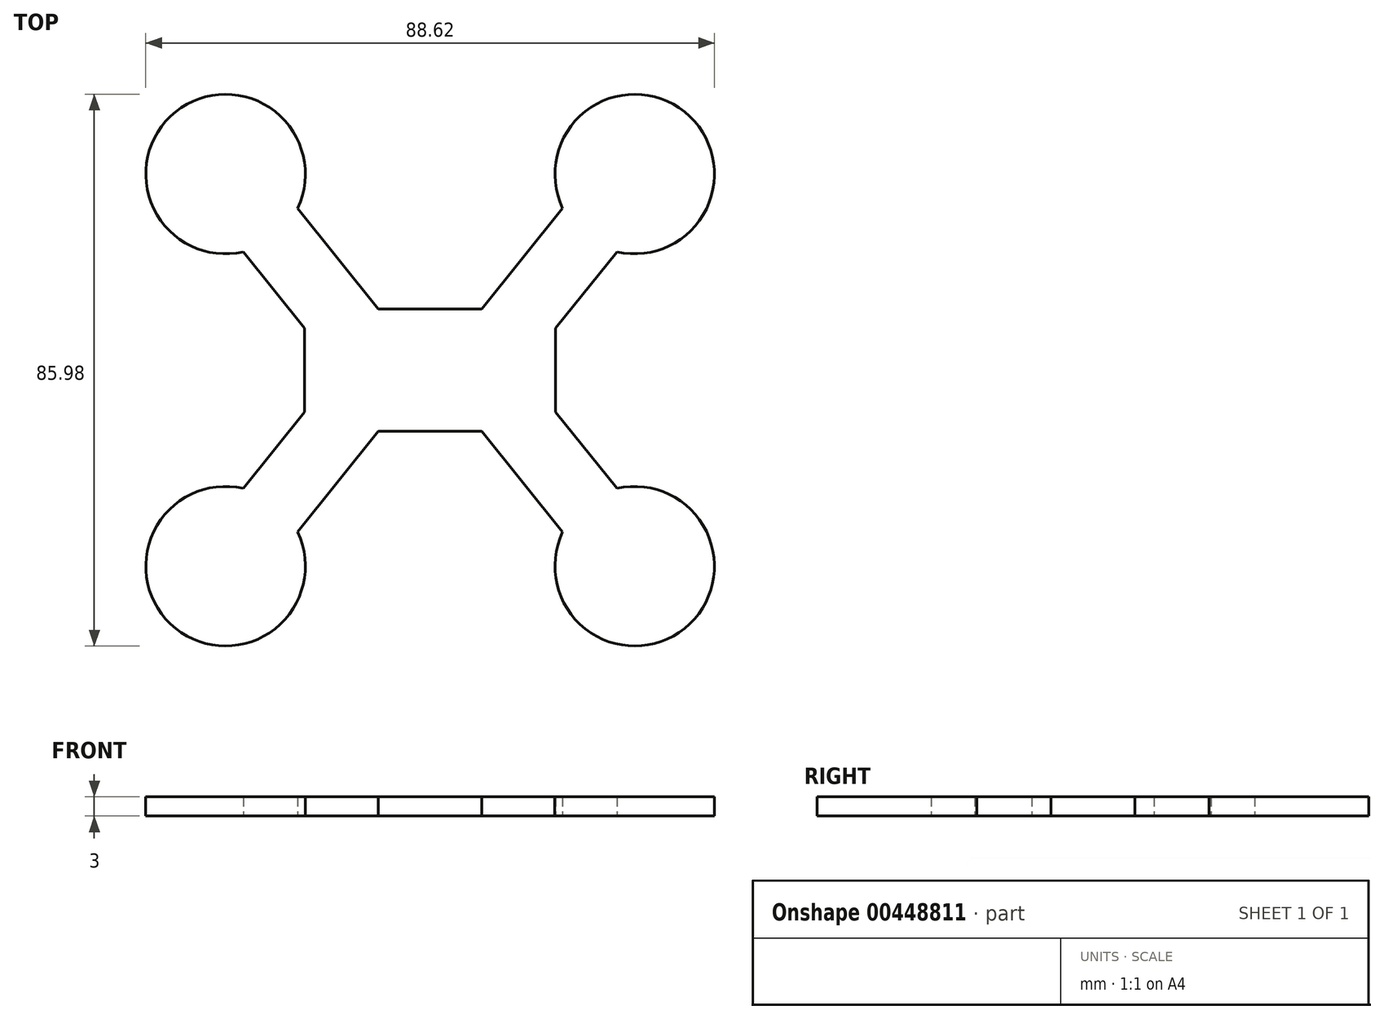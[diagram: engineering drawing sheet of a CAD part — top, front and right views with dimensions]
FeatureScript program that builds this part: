
annotation { "Feature Type Name" : "Feature", "Feature Type Description" : "" }
export const myFeature = defineFeature(function(context is Context, id is Id, definition is map)
    precondition{}
    {
        {
            var Q0;
            Q0=qCreatedBy(makeId("Top.planeOp"),FACE);
            var sketch = newSketch(context, id + "F0", { "sketchPlane" : qUnion([Q0])});
            skLineSegment(sketch, "E0", {"start": v(8.05, 9.53) * mm, "end": v(27.64, 33.95) * mm});
            skLineSegment(sketch, "E1", {"start": v(27.64, 33.95) * mm, "end": v(36.11, 27.16) * mm});
            skLineSegment(sketch, "E2", {"start": v(36.11, 27.16) * mm, "end": v(19.57, 6.54) * mm});
            skLineSegment(sketch, "E3", {"start": v(19.57, 6.54) * mm, "end": v(8.05, 9.53) * mm});
            skCircle(sketch, "E4", {"center": v(31.88, 30.56) * mm, "radius": 12.43 * mm});
            skLineSegment(sketch, "E5.MirrorCS", {"start": v(-27.64, 33.95) * mm, "end": v(-36.11, 27.16) * mm});
            skLineSegment(sketch, "E6.MirrorCS", {"start": v(-8.05, 9.53) * mm, "end": v(-27.64, 33.95) * mm});
            skLineSegment(sketch, "E7.MirrorCS", {"start": v(-19.57, 6.54) * mm, "end": v(-8.05, 9.53) * mm});
            skLineSegment(sketch, "E8.MirrorCS", {"start": v(-36.11, 27.16) * mm, "end": v(-19.57, 6.54) * mm});
            skCircle(sketch, "E9.MirrorC", {"center": v(-31.88, 30.56) * mm, "radius": 12.43 * mm});
            skLineSegment(sketch, "E10.MirrorCS", {"start": v(27.64, -33.95) * mm, "end": v(36.11, -27.16) * mm});
            skCircle(sketch, "E11.MirrorC", {"center": v(31.88, -30.56) * mm, "radius": 12.43 * mm});
            skLineSegment(sketch, "E12.MirrorCS", {"start": v(19.57, -6.54) * mm, "end": v(8.05, -9.53) * mm});
            skLineSegment(sketch, "E13.MirrorCS", {"start": v(36.11, -27.16) * mm, "end": v(19.57, -6.54) * mm});
            skLineSegment(sketch, "E14.MirrorCS", {"start": v(8.05, -9.53) * mm, "end": v(27.64, -33.95) * mm});
            skLineSegment(sketch, "E15.MirrorCS", {"start": v(-27.64, -33.95) * mm, "end": v(-36.11, -27.16) * mm});
            skLineSegment(sketch, "E16.MirrorCS", {"start": v(-36.11, -27.16) * mm, "end": v(-19.57, -6.54) * mm});
            skLineSegment(sketch, "E17.MirrorCS", {"start": v(-19.57, -6.54) * mm, "end": v(-8.05, -9.53) * mm});
            skCircle(sketch, "E18.MirrorC", {"center": v(-31.88, -30.56) * mm, "radius": 12.43 * mm});
            skLineSegment(sketch, "E19.MirrorCS", {"start": v(-8.05, -9.53) * mm, "end": v(-27.64, -33.95) * mm});
            skLineSegment(sketch, "E20.bottom", {"start": v(-19.57, 6.54) * mm, "end": v(19.57, 6.54) * mm});
            skLineSegment(sketch, "E20.top", {"start": v(-19.57, -6.54) * mm, "end": v(19.57, -6.54) * mm});
            skLineSegment(sketch, "E20.left", {"start": v(-19.57, 6.54) * mm, "end": v(-19.57, -6.54) * mm});
            skLineSegment(sketch, "E20.right", {"start": v(19.57, 6.54) * mm, "end": v(19.57, -6.54) * mm});
            skLineSegment(sketch, "E21.bottom", {"start": v(-8.05, 9.53) * mm, "end": v(8.05, 9.53) * mm});
            skLineSegment(sketch, "E21.top", {"start": v(-8.05, -9.53) * mm, "end": v(8.05, -9.53) * mm});
            skLineSegment(sketch, "E21.left", {"start": v(-8.05, 9.53) * mm, "end": v(-8.05, -9.53) * mm});
            skLineSegment(sketch, "E21.right", {"start": v(8.05, 9.53) * mm, "end": v(8.05, -9.53) * mm});
            skSolve(sketch);
        }
        {
            var Q0;
            {var subQ0=sQuery(id+"F0.wireOp",EDGE,"E5.MirrorCS");Q0=makeQuery(id+"F0.imprint","IMPRINT",FACE,{"disambiguationData":[TD([[makeQuery(id+"F0.imprint","IMPRINT",EDGE,{"derivedFrom":subQ0}),-1.0]])]});}
            var Q1;
            {var subQ0=sQuery(id+"F0.wireOp",EDGE,"E5.MirrorCS");Q1=makeQuery(id+"F0.imprint","IMPRINT",FACE,{"disambiguationData":[TD([[makeQuery(id+"F0.imprint","IMPRINT",EDGE,{"derivedFrom":subQ0}),1.0]])]});}
            var Q2;
            {var subQ5=sQuery(id+"F0.wireOp",EDGE,"E7.MirrorCS");Q2=makeQuery(id+"F0.imprint","IMPRINT",FACE,{"disambiguationData":[TD([[makeQuery(id+"F0.imprint","IMPRINT",EDGE,{"derivedFrom":subQ5}),1.0]])]});}
            var Q3;
            {var subQ0=sQuery(id+"F0.wireOp",EDGE,"E1");Q3=makeQuery(id+"F0.imprint","IMPRINT",FACE,{"disambiguationData":[TD([[makeQuery(id+"F0.imprint","IMPRINT",EDGE,{"derivedFrom":subQ0}),1.0]])]});}
            var Q4;
            {var subQ0=sQuery(id+"F0.wireOp",EDGE,"E1");Q4=makeQuery(id+"F0.imprint","IMPRINT",FACE,{"disambiguationData":[TD([[makeQuery(id+"F0.imprint","IMPRINT",EDGE,{"derivedFrom":subQ0}),-1.0]])]});}
            var Q5;
            {var subQ5=sQuery(id+"F0.wireOp",EDGE,"E3");Q5=makeQuery(id+"F0.imprint","IMPRINT",FACE,{"disambiguationData":[TD([[makeQuery(id+"F0.imprint","IMPRINT",EDGE,{"derivedFrom":subQ5}),-1.0]])]});}
            var Q6;
            {var subQ0=sQuery(id+"F0.wireOp",EDGE,"E10.MirrorCS");Q6=makeQuery(id+"F0.imprint","IMPRINT",FACE,{"disambiguationData":[TD([[makeQuery(id+"F0.imprint","IMPRINT",EDGE,{"derivedFrom":subQ0}),-1.0]])]});}
            var Q7;
            {var subQ0=sQuery(id+"F0.wireOp",EDGE,"E10.MirrorCS");Q7=makeQuery(id+"F0.imprint","IMPRINT",FACE,{"disambiguationData":[TD([[makeQuery(id+"F0.imprint","IMPRINT",EDGE,{"derivedFrom":subQ0}),1.0]])]});}
            var Q8;
            {var subQ0=sQuery(id+"F0.wireOp",EDGE,"E12.MirrorCS");Q8=makeQuery(id+"F0.imprint","IMPRINT",FACE,{"disambiguationData":[TD([[makeQuery(id+"F0.imprint","IMPRINT",EDGE,{"derivedFrom":subQ0}),1.0]])]});}
            var Q9;
            {var subQ0=sQuery(id+"F0.wireOp",EDGE,"E15.MirrorCS");Q9=makeQuery(id+"F0.imprint","IMPRINT",FACE,{"disambiguationData":[TD([[makeQuery(id+"F0.imprint","IMPRINT",EDGE,{"derivedFrom":subQ0}),1.0]])]});}
            var Q10;
            {var subQ0=sQuery(id+"F0.wireOp",EDGE,"E15.MirrorCS");Q10=makeQuery(id+"F0.imprint","IMPRINT",FACE,{"disambiguationData":[TD([[makeQuery(id+"F0.imprint","IMPRINT",EDGE,{"derivedFrom":subQ0}),-1.0]])]});}
            var Q11;
            {var subQ5=sQuery(id+"F0.wireOp",EDGE,"E17.MirrorCS");Q11=makeQuery(id+"F0.imprint","IMPRINT",FACE,{"disambiguationData":[TD([[makeQuery(id+"F0.imprint","IMPRINT",EDGE,{"derivedFrom":subQ5}),-1.0]])]});}
            var Q12;
            {var subQ0=sQuery(id+"F0.wireOp",EDGE,"E20.left");Q12=makeQuery(id+"F0.imprint","IMPRINT",FACE,{"disambiguationData":[TD([[makeQuery(id+"F0.imprint","IMPRINT",EDGE,{"derivedFrom":subQ0}),1.0]])]});}
            var Q13;
            {var subQ0=sQuery(id+"F0.wireOp",EDGE,"E21.left");var subQ1=sQuery(id+"F0.wireOp",EDGE,"E20.bottom");var subQ2=makeQuery(id+"F0.imprint","INTERSECT",VERTEX,{"derivedFrom":[subQ1,subQ0]});Q13=makeQuery(id+"F0.imprint","IMPRINT",FACE,{"disambiguationData":[TD([[makeQuery(id+"F0.imprint","IMPRINT",EDGE,{"disambiguationData":[TD([[subQ2,-1.0]])],"derivedFrom":subQ1}),-1.0]])]});}
            var Q14;
            {var subQ0=sQuery(id+"F0.wireOp",EDGE,"E20.right");Q14=makeQuery(id+"F0.imprint","IMPRINT",FACE,{"disambiguationData":[TD([[makeQuery(id+"F0.imprint","IMPRINT",EDGE,{"derivedFrom":subQ0}),-1.0]])]});}
            var Q15;
            {var subQ5=sQuery(id+"F0.wireOp",EDGE,"E21.top");Q15=makeQuery(id+"F0.imprint","IMPRINT",FACE,{"disambiguationData":[TD([[makeQuery(id+"F0.imprint","IMPRINT",EDGE,{"derivedFrom":subQ5}),1.0]])]});}
            var Q16;
            {var subQ5=sQuery(id+"F0.wireOp",EDGE,"E21.bottom");Q16=makeQuery(id+"F0.imprint","IMPRINT",FACE,{"disambiguationData":[TD([[makeQuery(id+"F0.imprint","IMPRINT",EDGE,{"derivedFrom":subQ5}),-1.0]])]});}
            var Q17;
            {var subQ0=sQuery(id+"F0.wireOp",EDGE,"E7.MirrorCS");Q17=makeQuery(id+"F0.imprint","IMPRINT",FACE,{"disambiguationData":[TD([[makeQuery(id+"F0.imprint","IMPRINT",EDGE,{"derivedFrom":subQ0}),-1.0]])]});}
            var Q18;
            {var subQ0=sQuery(id+"F0.wireOp",EDGE,"E17.MirrorCS");Q18=makeQuery(id+"F0.imprint","IMPRINT",FACE,{"disambiguationData":[TD([[makeQuery(id+"F0.imprint","IMPRINT",EDGE,{"derivedFrom":subQ0}),1.0]])]});}
            var Q19;
            {var subQ0=sQuery(id+"F0.wireOp",EDGE,"E12.MirrorCS");Q19=makeQuery(id+"F0.imprint","IMPRINT",FACE,{"disambiguationData":[TD([[makeQuery(id+"F0.imprint","IMPRINT",EDGE,{"derivedFrom":subQ0}),-1.0]])]});}
            var Q20;
            {var subQ0=sQuery(id+"F0.wireOp",EDGE,"E3");Q20=makeQuery(id+"F0.imprint","IMPRINT",FACE,{"disambiguationData":[TD([[makeQuery(id+"F0.imprint","IMPRINT",EDGE,{"derivedFrom":subQ0}),1.0]])]});}
            extrude(context, id + "F1", {"entities" : qUnion([Q0, Q1, Q2, Q3, Q4, Q5, Q6, Q7, Q8, Q9, Q10, Q11, Q12, Q13, Q14, Q15, Q16, Q17, Q18, Q19, Q20]), "depth" : 3 * mm});
        }
    });
